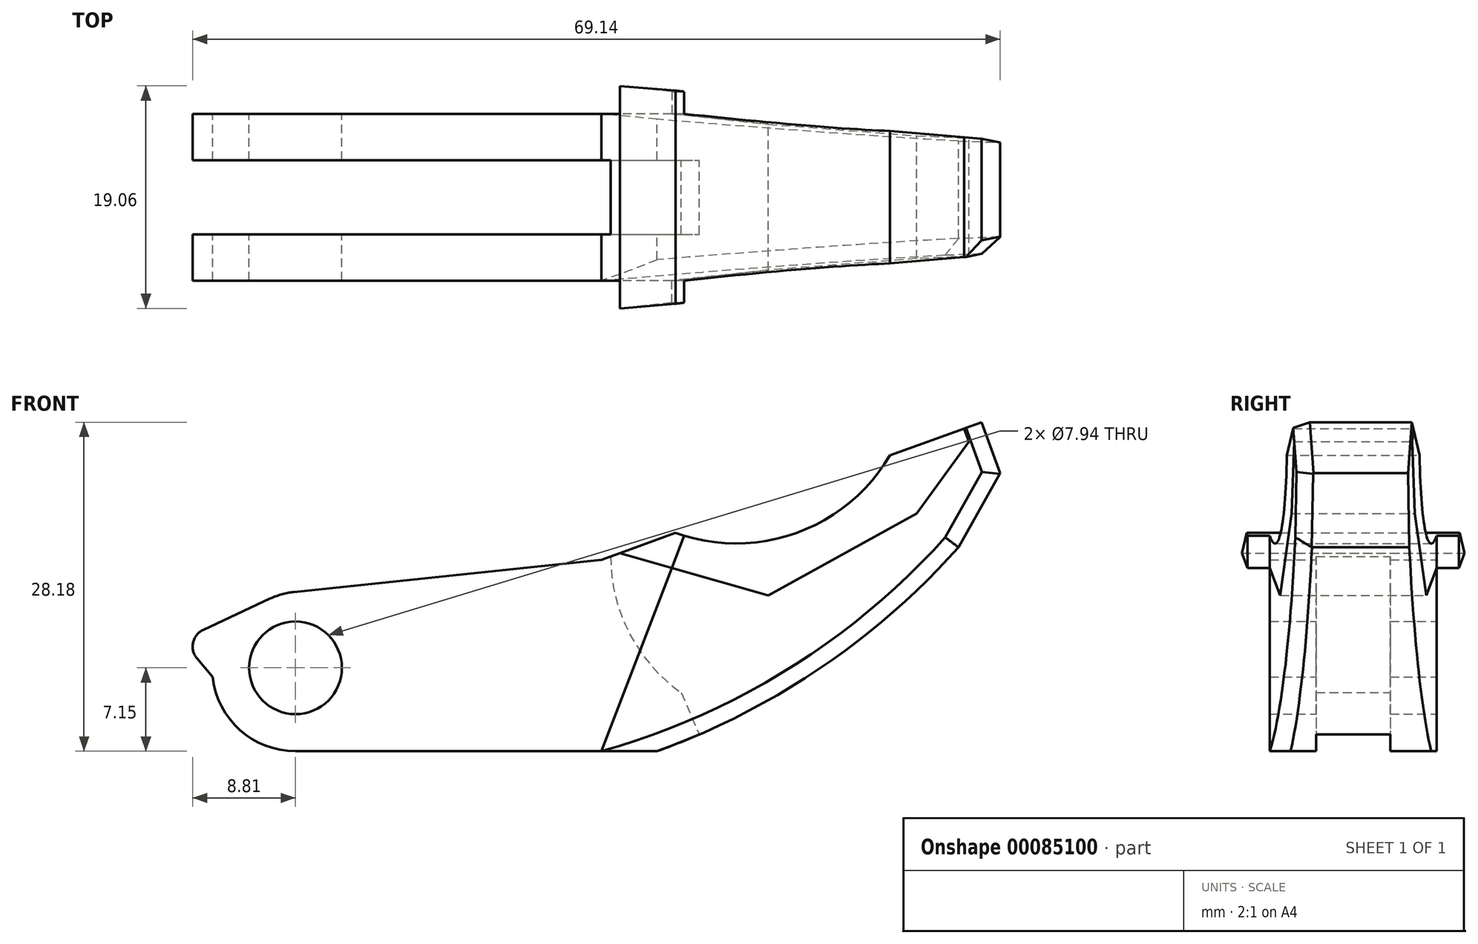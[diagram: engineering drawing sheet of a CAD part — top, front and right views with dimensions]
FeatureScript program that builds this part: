
annotation { "Feature Type Name" : "Feature", "Feature Type Description" : "" }
export const myFeature = defineFeature(function(context is Context, id is Id, definition is map)
    precondition{}
    {
        {
            var Q0;
            Q0=qCreatedBy(makeId("Front.planeOp"),FACE);
            var sketch = newSketch(context, id + "F0", { "sketchPlane" : qUnion([Q0])});
            skCircle(sketch, "E0", {"center": v(0, 0) * mm, "radius": 3.97 * mm});
            skLineSegment(sketch, "E1", {"start": v(0, -7.14) * mm, "end": v(30.96, -7.14) * mm});
            skLineSegment(sketch, "E2", {"start": v(18.9, 0) * mm, "end": v(-17.1, 0) * mm, "construction": true});
            skLineSegment(sketch, "E3", {"start": v(-7.1, -0.8) * mm, "end": v(-8.43, 0.8) * mm});
            skLineSegment(sketch, "E4", {"start": v(-7.89, 3.26) * mm, "end": v(-1.2, 6.38) * mm});
            skLineSegment(sketch, "E5", {"start": v(-9.76, 2.38) * mm, "end": v(-20.6, -2.68) * mm, "construction": true});
            skLineSegment(sketch, "E6", {"start": v(3.23, -13.1) * mm, "end": v(-16.98, 10.98) * mm, "construction": true});
            skArc(sketch, "E7", {"start": v(-7.89, 3.26) * mm, "mid": v(-8.77, 2.16) * mm, "end": v(-8.43, 0.8) * mm});
            skLineSegment(sketch, "E8", {"start": v(-9.76, 2.38) * mm, "end": v(-7.89, 3.26) * mm, "construction": true});
            skLineSegment(sketch, "E9", {"start": v(0, -13.35) * mm, "end": v(0, 12.74) * mm, "construction": true});
            skArc(sketch, "E10", {"start": v(-7.1, -0.8) * mm, "mid": v(-4.76, -5.32) * mm, "end": v(0, -7.14) * mm});
            skLineSegment(sketch, "E11", {"start": v(-1.2, 6.38) * mm, "end": v(26.2, 9.26) * mm});
            skPoint(sketch, "E12", {"position": v(-1.2, 6.38) * mm});
            skLineSegment(sketch, "E13", {"start": v(26.2, -7.14) * mm, "end": v(32.22, 8.56) * mm, "construction": true});
            skLineSegment(sketch, "E14", {"start": v(30.96, -7.14) * mm, "end": v(87.34, -7.14) * mm, "construction": true});
            skLineSegment(sketch, "E15", {"start": v(40.48, 6.19) * mm, "end": v(32.22, 8.56) * mm});
            skLineSegment(sketch, "E16", {"start": v(40.48, 6.19) * mm, "end": v(53.18, 13.23) * mm});
            skLineSegment(sketch, "E17", {"start": v(26.2, 9.26) * mm, "end": v(32.54, 11.55) * mm});
            skLineSegment(sketch, "E18", {"start": v(27.78, 9.83) * mm, "end": v(32.22, 8.56) * mm});
            skLineSegment(sketch, "E19", {"start": v(32.54, 11.55) * mm, "end": v(50.9, 18.2) * mm, "construction": true});
            skArc(sketch, "E20", {"start": v(32.54, 11.55) * mm, "mid": v(42.93, 11.55) * mm, "end": v(50.9, 18.2) * mm});
            skLineSegment(sketch, "E21", {"start": v(57.25, 20.5) * mm, "end": v(50.9, 18.2) * mm});
            skArc(sketch, "E22", {"start": v(30.96, -7.14) * mm, "mid": v(44.94, -0.02) * mm, "end": v(56.75, 10.32) * mm});
            skPoint(sketch, "E23.orphan", {"position": v(56.75, -7.14) * mm});
            skLineSegment(sketch, "E24", {"start": v(56.75, -7.14) * mm, "end": v(56.75, 10.32) * mm, "construction": true});
            skLineSegment(sketch, "E25", {"start": v(53.18, 13.23) * mm, "end": v(57.66, 19.37) * mm});
            skLineSegment(sketch, "E26", {"start": v(57.25, 20.5) * mm, "end": v(58.75, 21.03) * mm});
            skLineSegment(sketch, "E27", {"start": v(57.25, 20.5) * mm, "end": v(57.66, 19.37) * mm});
            skLineSegment(sketch, "E28", {"start": v(58.75, 21.03) * mm, "end": v(60.33, 16.67) * mm});
            skLineSegment(sketch, "E29", {"start": v(60.33, 16.67) * mm, "end": v(56.75, 10.32) * mm});
            skSolve(sketch);
        }
        {
            var Q0;
            Q0=qCreatedBy(makeId("Front.planeOp"),FACE);
            var sketch = newSketch(context, id + "F1", { "sketchPlane" : qUnion([Q0])});
            skArc(sketch, "E30", {"start": v(27.22, 12.1) * mm, "mid": v(28.04, 4.14) * mm, "end": v(33.02, -2.14) * mm});
            skLineSegment(sketch, "E31", {"start": v(33.02, -2.14) * mm, "end": v(39.27, -16.57) * mm});
            skLineSegment(sketch, "E32", {"start": v(39.27, -16.57) * mm, "end": v(-29.8, -16.57) * mm});
            skLineSegment(sketch, "E33", {"start": v(-29.8, -16.57) * mm, "end": v(-29.8, 12.1) * mm});
            skLineSegment(sketch, "E34", {"start": v(-29.8, 12.1) * mm, "end": v(27.22, 12.1) * mm});
            skSolve(sketch);
        }
        {
            var Q0;
            Q0=makeQuery(id+"F0.imprint","IMPRINT",FACE,{"disambiguationData":[TD([[makeQuery(id+"F0.imprint","IMPRINT",EDGE,{"derivedFrom":sQuery(id+"F0.wireOp",EDGE,"E0")}),-1.0]])]});
            extrude(context, id + "F2", {"entities" : qUnion([Q0]), "endBound" : BoundingType.SYMMETRIC, "depth" : 14.29 * mm});
        }
        {
            var Q0;
            Q0=makeQuery(id+"F0.imprint","IMPRINT",FACE,{"disambiguationData":[TD([[makeQuery(id+"F0.imprint","IMPRINT",EDGE,{"derivedFrom":sQuery(id+"F0.wireOp",EDGE,"E15")}),-1.0]])]});
            extrude(context, id + "F3", {"entities" : qUnion([Q0]), "endBound" : BoundingType.SYMMETRIC, "depth" : 19.05 * mm});
        }
        {
            var Q0;
            Q0=makeQuery(id+"F2.opExtrude","SWEPT_EDGE",EDGE,{"disambiguationData":[OSD([sQuery(id+"F0.wireOp",EDGE,"E4"),sQuery(id+"F0.wireOp",EDGE,"E11")])]});
            fillet(context, id + "F4", {"entities" : qUnion([Q0]), "radius" : 6.35 * mm, "tangentPropagation" : true, "allowEdgeOverflow" : false});
        }
        {
            var Q0;
            Q0=sQuery(id+"F0.wireOp",VERTEX,"E13.start");
            var Q1;
            Q1=sQuery(id+"F0.wireOp",EDGE,"E13");
            cPlane(context, id + "F5", {"entities" : qUnion([Q0, Q1]), "cplaneType" : CPlaneType.LINE_POINT, "offset" : 152.4 * mm, "width" : 152.4 * mm, "height" : 152.4 * mm});
        }
        {
            var Q0;
            Q0=qCreatedBy(id+"F5.planeOp",FACE);
            var sketch = newSketch(context, id + "F6", { "sketchPlane" : qUnion([Q0])});
            skPoint(sketch, "E35.startSnap0", {"position": v(31.46, 0) * mm});
            skLineSegment(sketch, "E36", {"start": v(22.41, -9.53) * mm, "end": v(70.07, -4.52) * mm});
            skLineSegment(sketch, "E37", {"start": v(22.41, -9.53) * mm, "end": v(22.41, -23.14) * mm});
            skLineSegment(sketch, "E38", {"start": v(22.41, -23.14) * mm, "end": v(70.44, -23.14) * mm});
            skLineSegment(sketch, "E39", {"start": v(70.44, -23.14) * mm, "end": v(70.07, -4.52) * mm});
            skSolve(sketch);
        }
        {
            var Q0;
            Q0=qCreatedBy(id+"F5.planeOp",FACE);
            var sketch = newSketch(context, id + "F7", { "sketchPlane" : qUnion([Q0])});
            skLineSegment(sketch, "E40", {"start": v(27.01, 0) * mm, "end": v(27.01, 29.64) * mm, "construction": true});
            skLineSegment(sketch, "E41", {"start": v(27.01, -7.14) * mm, "end": v(84.88, -1.06) * mm});
            skLineSegment(sketch, "E42", {"start": v(27.01, -7.14) * mm, "end": v(27.01, -18.15) * mm});
            skLineSegment(sketch, "E43", {"start": v(27.01, -18.15) * mm, "end": v(84.88, -18.15) * mm});
            skLineSegment(sketch, "E44", {"start": v(84.88, -18.15) * mm, "end": v(84.88, -1.06) * mm});
            skSolve(sketch);
        }
        {
            var Q0;
            Q0=makeQuery(id+"F7.imprint","IMPRINT",FACE,{"disambiguationData":[TD([[makeQuery(id+"F7.imprint","IMPRINT",EDGE,{"derivedFrom":sQuery(id+"F7.wireOp",EDGE,"E41")}),-1.0]])]});
            extrude(context, id + "F8", {"entities" : qUnion([Q0]), "operationType" : NewBodyOperationType.REMOVE, "depth" : 40.95 * mm});
        }
        {
            var Q0;
            Q0=makeQuery(id+"F6.imprint","IMPRINT",FACE,{"disambiguationData":[TD([[makeQuery(id+"F6.imprint","IMPRINT",EDGE,{"derivedFrom":sQuery(id+"F6.wireOp",EDGE,"E36")}),-1.0]])]});
            extrude(context, id + "F9", {"entities" : qUnion([Q0]), "operationType" : NewBodyOperationType.REMOVE, "depth" : 46.4 * mm});
        }
        {
            var Q0;
            Q0=makeQuery(id+"F2.opExtrude","SWEPT_BODY",BODY,{"disambiguationData":[OSD([sQuery(id+"F0.wireOp",EDGE,"E0"),sQuery(id+"F0.wireOp",EDGE,"E1"),sQuery(id+"F0.wireOp",EDGE,"E3"),sQuery(id+"F0.wireOp",EDGE,"E4"),sQuery(id+"F0.wireOp",EDGE,"E7"),sQuery(id+"F0.wireOp",EDGE,"E10"),sQuery(id+"F0.wireOp",EDGE,"E11"),sQuery(id+"F0.wireOp",EDGE,"E15"),sQuery(id+"F0.wireOp",EDGE,"E16"),sQuery(id+"F0.wireOp",EDGE,"E17"),sQuery(id+"F0.wireOp",EDGE,"E18"),sQuery(id+"F0.wireOp",EDGE,"E22"),sQuery(id+"F0.wireOp",EDGE,"E25"),sQuery(id+"F0.wireOp",EDGE,"E26"),sQuery(id+"F0.wireOp",EDGE,"E27"),sQuery(id+"F0.wireOp",EDGE,"E28"),sQuery(id+"F0.wireOp",EDGE,"E29")])]});
            var Q1;
            Q1=makeQuery(id+"F3.opExtrude","SWEPT_BODY",BODY,{"disambiguationData":[OSD([sQuery(id+"F0.wireOp",EDGE,"E15"),sQuery(id+"F0.wireOp",EDGE,"E16"),sQuery(id+"F0.wireOp",EDGE,"E17"),sQuery(id+"F0.wireOp",EDGE,"E18"),sQuery(id+"F0.wireOp",EDGE,"E20"),sQuery(id+"F0.wireOp",EDGE,"E21"),sQuery(id+"F0.wireOp",EDGE,"E25"),sQuery(id+"F0.wireOp",EDGE,"E27")])]});
            var Q2;
            Q2=qCreatedBy(makeId("Front.planeOp"),FACE);
            mirror(context, id + "F10", {"operationType" : NewBodyOperationType.INTERSECT, "entities" : qUnion([Q0, Q1]), "mirrorPlane" : qUnion([Q2])});
        }
        {
            var Q0;
            Q0=makeQuery(id+"F1.imprint","IMPRINT",FACE,{"disambiguationData":[TD([[makeQuery(id+"F1.imprint","IMPRINT",EDGE,{"derivedFrom":sQuery(id+"F1.wireOp",EDGE,"E30")}),-1.0]])]});
            extrude(context, id + "F11", {"entities" : qUnion([Q0]), "operationType" : NewBodyOperationType.REMOVE, "endBound" : BoundingType.SYMMETRIC, "depth" : 6.35 * mm});
        }
        {
            var Q0;
            Q0=makeQuery(id+"F8.boolean.opBoolean","COPY",EDGE,{"derivedFrom":makeQuery(id+"F8.opExtrude","CAP_EDGE",EDGE,{"disambiguationData":[OSD([sQuery(id+"F7.wireOp",EDGE,"E41")])],"isStart":true})});
            var Q1;
            Q1=makeQuery(id+"F8.boolean.opBoolean","INTERSECT",EDGE,{"derivedFrom":[makeQuery(id+"F2.opExtrude","SWEPT_FACE",FACE,{"disambiguationData":[OSD([sQuery(id+"F0.wireOp",EDGE,"E22")])]}),makeQuery(id+"F8.opExtrude","SWEPT_FACE",FACE,{"disambiguationData":[OSD([sQuery(id+"F7.wireOp",EDGE,"E41")])]})]});
            var Q2;
            Q2=makeQuery(id+"F8.boolean.opBoolean","INTERSECT",EDGE,{"derivedFrom":[makeQuery(id+"F2.opExtrude","SWEPT_FACE",FACE,{"disambiguationData":[OSD([sQuery(id+"F0.wireOp",EDGE,"E29")])]}),makeQuery(id+"F8.opExtrude","SWEPT_FACE",FACE,{"disambiguationData":[OSD([sQuery(id+"F7.wireOp",EDGE,"E41")])]})]});
            var Q3;
            Q3=makeQuery(id+"F8.boolean.opBoolean","INTERSECT",EDGE,{"derivedFrom":[makeQuery(id+"F2.opExtrude","SWEPT_FACE",FACE,{"disambiguationData":[OSD([sQuery(id+"F0.wireOp",EDGE,"E28")])]}),makeQuery(id+"F8.opExtrude","SWEPT_FACE",FACE,{"disambiguationData":[OSD([sQuery(id+"F7.wireOp",EDGE,"E41")])]})]});
            var Q4;
            Q4=makeQuery(id+"F10.boolean.opBoolean","COPY",EDGE,{"derivedFrom":makeQuery(id+"F10.boolean.toolComplement.opBoolean","COPY",EDGE,{"derivedFrom":makeQuery(id+"F10.opPattern","COPY",EDGE,{"derivedFrom":makeQuery(id+"F8.boolean.opBoolean","INTERSECT",EDGE,{"derivedFrom":[makeQuery(id+"F2.opExtrude","SWEPT_FACE",FACE,{"disambiguationData":[OSD([sQuery(id+"F0.wireOp",EDGE,"E28")])]}),makeQuery(id+"F8.opExtrude","SWEPT_FACE",FACE,{"disambiguationData":[OSD([sQuery(id+"F7.wireOp",EDGE,"E41")])]})]}),"instanceName":"1"})})});
            var Q5;
            Q5=makeQuery(id+"F10.boolean.opBoolean","COPY",EDGE,{"derivedFrom":makeQuery(id+"F10.boolean.toolComplement.opBoolean","COPY",EDGE,{"derivedFrom":makeQuery(id+"F10.opPattern","COPY",EDGE,{"derivedFrom":makeQuery(id+"F8.boolean.opBoolean","INTERSECT",EDGE,{"derivedFrom":[makeQuery(id+"F2.opExtrude","SWEPT_FACE",FACE,{"disambiguationData":[OSD([sQuery(id+"F0.wireOp",EDGE,"E29")])]}),makeQuery(id+"F8.opExtrude","SWEPT_FACE",FACE,{"disambiguationData":[OSD([sQuery(id+"F7.wireOp",EDGE,"E41")])]})]}),"instanceName":"1"})})});
            var Q6;
            Q6=makeQuery(id+"F10.boolean.opBoolean","COPY",EDGE,{"derivedFrom":makeQuery(id+"F10.boolean.toolComplement.opBoolean","COPY",EDGE,{"derivedFrom":makeQuery(id+"F10.opPattern","COPY",EDGE,{"derivedFrom":makeQuery(id+"F8.boolean.opBoolean","INTERSECT",EDGE,{"derivedFrom":[makeQuery(id+"F2.opExtrude","SWEPT_FACE",FACE,{"disambiguationData":[OSD([sQuery(id+"F0.wireOp",EDGE,"E22")])]}),makeQuery(id+"F8.opExtrude","SWEPT_FACE",FACE,{"disambiguationData":[OSD([sQuery(id+"F7.wireOp",EDGE,"E41")])]})]}),"instanceName":"1"})})});
            var Q7;
            Q7=makeQuery(id+"F10.boolean.opBoolean","COPY",EDGE,{"derivedFrom":makeQuery(id+"F10.boolean.toolComplement.opBoolean","COPY",EDGE,{"derivedFrom":makeQuery(id+"F10.opPattern","COPY",EDGE,{"derivedFrom":makeQuery(id+"F8.boolean.opBoolean","COPY",EDGE,{"derivedFrom":makeQuery(id+"F8.opExtrude","CAP_EDGE",EDGE,{"disambiguationData":[OSD([sQuery(id+"F7.wireOp",EDGE,"E41")])],"isStart":true})}),"instanceName":"1"})})});
            chamfer(context, id + "F12", {"entities" : qUnion([Q0, Q1, Q2, Q3, Q4, Q5, Q6, Q7]), "chamferType" : ChamferType.OFFSET_ANGLE, "width" : 1.27 * mm, "oppositeDirection" : false, "angle" : 45 * degree, "tangentPropagation" : true});
        }
    });
